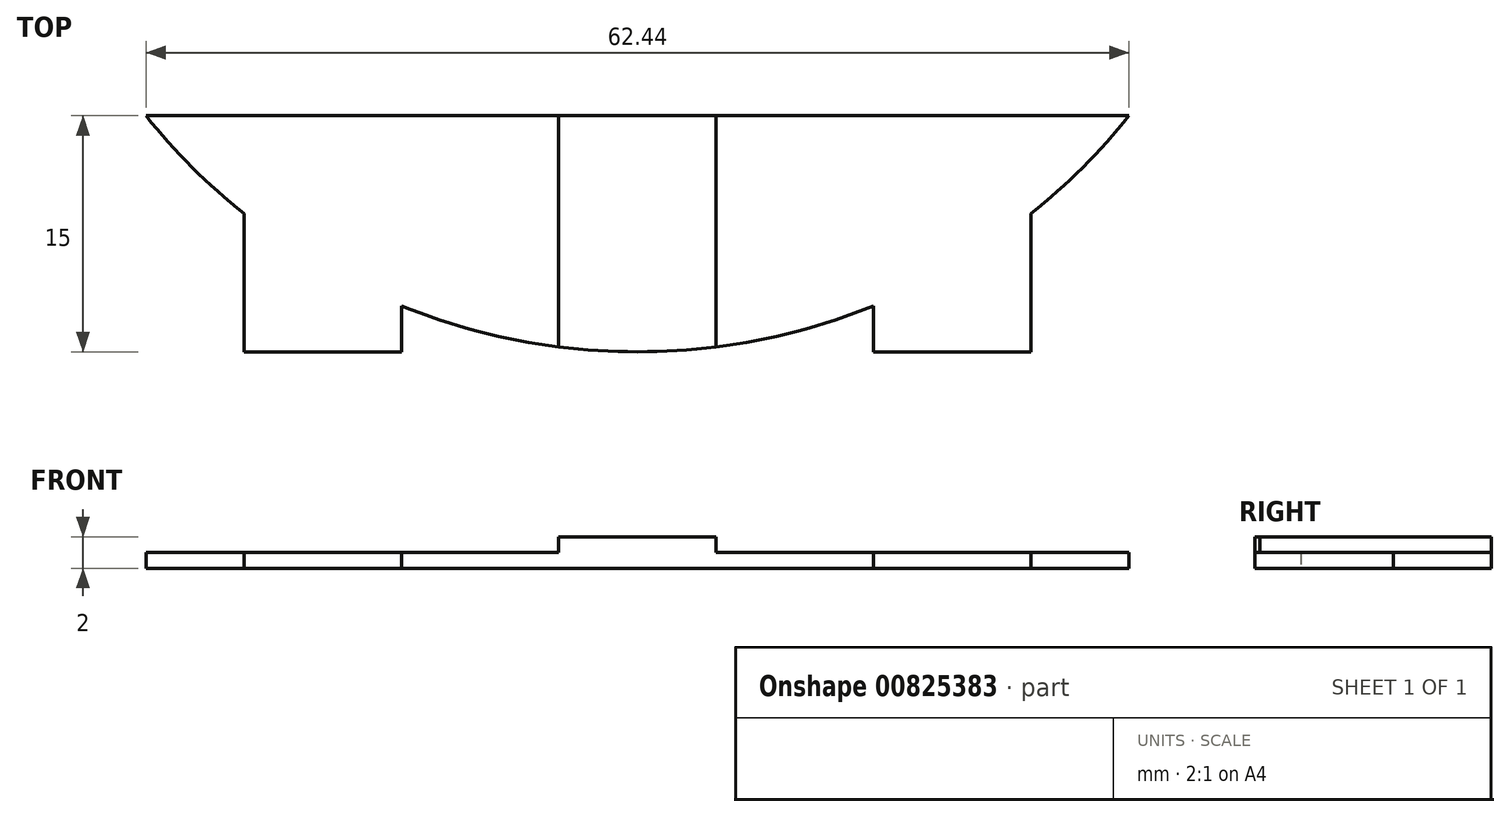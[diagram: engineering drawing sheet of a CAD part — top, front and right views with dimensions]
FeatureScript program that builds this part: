
annotation { "Feature Type Name" : "Feature", "Feature Type Description" : "" }
export const myFeature = defineFeature(function(context is Context, id is Id, definition is map)
    precondition{}
    {
        {
            var Q0;
            Q0=qCreatedBy(makeId("Top.planeOp"),FACE);
            var sketch = newSketch(context, id + "F0", { "sketchPlane" : qUnion([Q0])});
            skArc(sketch, "E0", {"start": v(-31.22, -25) * mm, "mid": v(-28.28, -28.28) * mm, "end": v(-25, -31.22) * mm});
            skLineSegment(sketch, "E1", {"start": v(0, -40) * mm, "end": v(0, -25) * mm, "construction": true});
            skLineSegment(sketch, "E2", {"start": v(-31.22, -25) * mm, "end": v(31.22, -25) * mm});
            skLineSegment(sketch, "E3", {"start": v(0, -40) * mm, "end": v(-15, -40) * mm, "construction": true});
            skLineSegment(sketch, "E4", {"start": v(0, -40) * mm, "end": v(15, -40) * mm, "construction": true});
            skLineSegment(sketch, "E5", {"start": v(-31.22, -25) * mm, "end": v(-31.22, -40) * mm, "construction": true});
            skLineSegment(sketch, "E6.bottom", {"start": v(-15, -40) * mm, "end": v(-25, -40) * mm});
            skLineSegment(sketch, "E6.top", {"start": v(-15, -40) * mm, "end": v(-25, -40) * mm});
            skLineSegment(sketch, "E6.left", {"start": v(-15, -40) * mm, "end": v(-15, -40) * mm});
            skLineSegment(sketch, "E6.right", {"start": v(-25, -40) * mm, "end": v(-25, -40) * mm});
            skLineSegment(sketch, "E7", {"start": v(-25, -40) * mm, "end": v(-25, -31.22) * mm});
            skLineSegment(sketch, "E8", {"start": v(-15, -40) * mm, "end": v(-15, -37.08) * mm});
            skLineSegment(sketch, "E9", {"start": v(15, -40) * mm, "end": v(15, -37.08) * mm});
            skLineSegment(sketch, "E10", {"start": v(15, -40) * mm, "end": v(25, -40) * mm});
            skLineSegment(sketch, "E11", {"start": v(25, -40) * mm, "end": v(25, -31.22) * mm});
            skArc(sketch, "E12.trimOffspring", {"start": v(-15, -37.08) * mm, "mid": v(0, -40) * mm, "end": v(15, -37.08) * mm});
            skArc(sketch, "E13.trimOffspring", {"start": v(25, -31.22) * mm, "mid": v(28.28, -28.28) * mm, "end": v(31.22, -25) * mm});
            skSolve(sketch);
        }
        {
            var Q0;
            Q0 = qSketchRegion(id + "F0", true);
            extrude(context, id + "F1", {"entities" : qUnion([Q0]), "depth" : 1 * mm, "offsetDistance" : 25 * mm});
        }
        {
            var Q0;
            Q0=makeQuery(id+"F1.opExtrude","CAP_FACE",FACE,{"disambiguationData":[OSD([sQuery(id+"F0.wireOp",EDGE,"E0"),sQuery(id+"F0.wireOp",EDGE,"E2"),sQuery(id+"F0.wireOp",EDGE,"E6.top"),sQuery(id+"F0.wireOp",EDGE,"E7"),sQuery(id+"F0.wireOp",EDGE,"E8"),sQuery(id+"F0.wireOp",EDGE,"E9"),sQuery(id+"F0.wireOp",EDGE,"E10"),sQuery(id+"F0.wireOp",EDGE,"E11"),sQuery(id+"F0.wireOp",EDGE,"E12.trimOffspring"),sQuery(id+"F0.wireOp",EDGE,"E13.trimOffspring")])],"isStart":false});
            var sketch = newSketch(context, id + "F2", { "sketchPlane" : qUnion([Q0])});
            skPoint(sketch, "E14.endSnap0", {"position": v(0, -40) * mm});
            skPoint(sketch, "E15.second.point", {"position": v(6.02, 30.24) * mm});
            skPoint(sketch, "E15.third.point", {"position": v(6.8, 30.56) * mm});
            skLineSegment(sketch, "E16", {"start": v(-5, -25) * mm, "end": v(-5, -39.69) * mm});
            skLineSegment(sketch, "E17", {"start": v(5, -25) * mm, "end": v(5, -39.69) * mm});
            skLineSegment(sketch, "E18", {"start": v(-5, -25) * mm, "end": v(5, -25) * mm});
            skArc(sketch, "E19", {"start": v(-5, -39.69) * mm, "mid": v(0, -40) * mm, "end": v(5, -39.69) * mm});
            skSolve(sketch);
        }
        {
            var Q0;
            Q0 = qSketchRegion(id + "F2", true);
            extrude(context, id + "F3", {"entities" : qUnion([Q0]), "operationType" : NewBodyOperationType.ADD, "depth" : 1 * mm, "offsetDistance" : 25 * mm});
        }
    });
